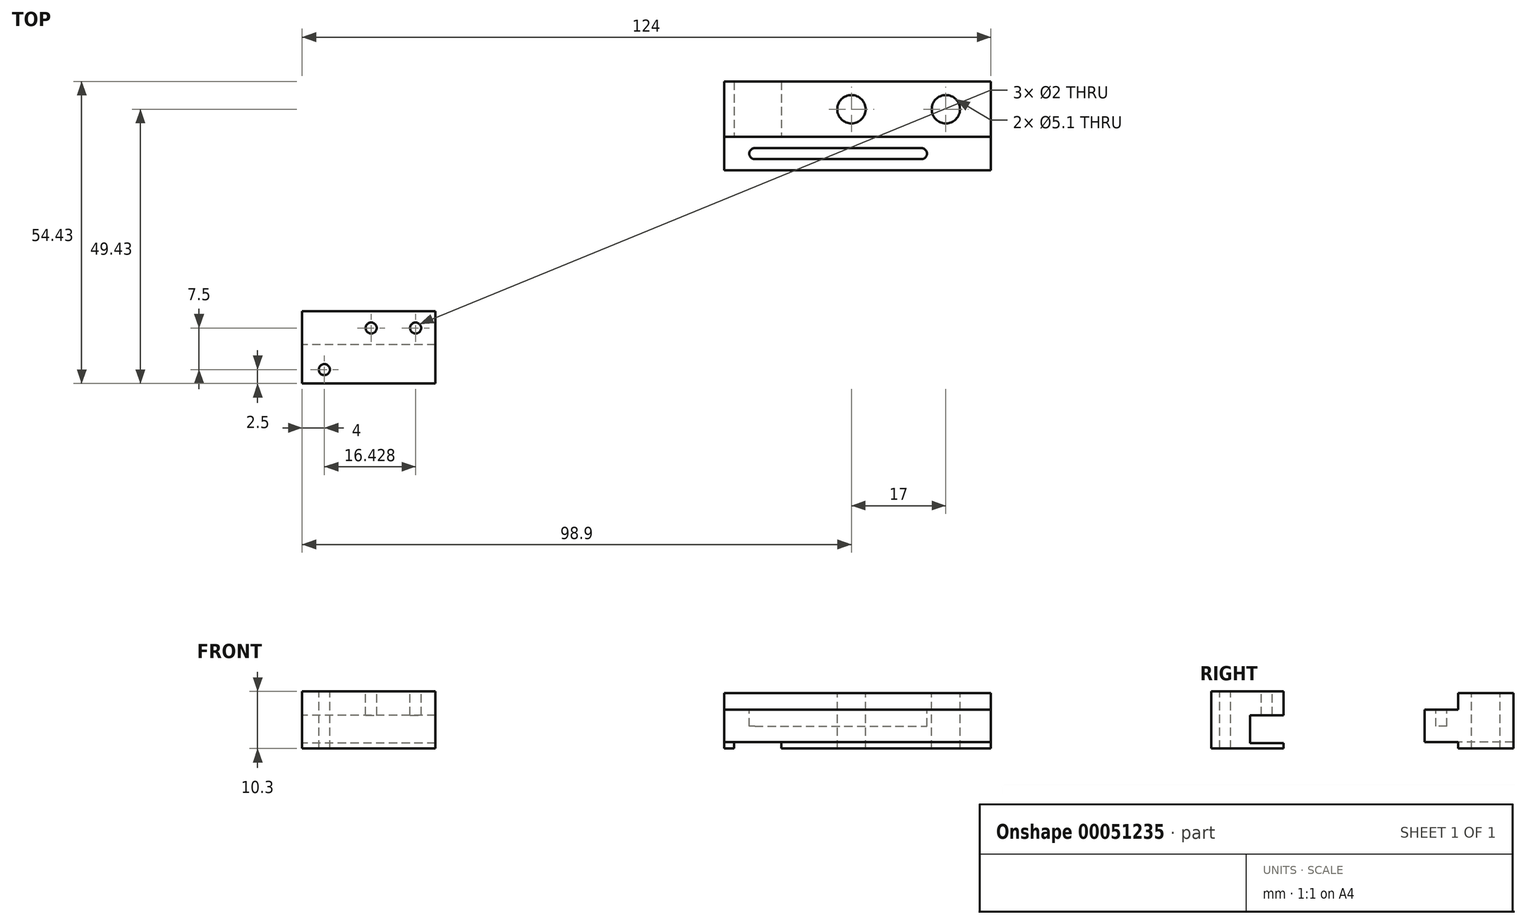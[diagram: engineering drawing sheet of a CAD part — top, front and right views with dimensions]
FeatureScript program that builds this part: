
annotation { "Feature Type Name" : "Feature", "Feature Type Description" : "" }
export const myFeature = defineFeature(function(context is Context, id is Id, definition is map)
    precondition{}
    {
        {
            var Q0;
            Q0=qCreatedBy(makeId("Right.planeOp"),FACE);
            var sketch = newSketch(context, id + "F0", { "sketchPlane" : qUnion([Q0])});
            skLineSegment(sketch, "E0", {"start": v(8, 0) * mm, "end": v(-2, 0) * mm});
            skLineSegment(sketch, "E1.0", {"start": v(8, 10) * mm, "end": v(-2, 10) * mm});
            skLineSegment(sketch, "E2", {"start": v(0, 0) * mm, "end": v(0, 15.1) * mm, "construction": true});
            skLineSegment(sketch, "E3.0", {"start": v(-8, 1.15) * mm, "end": v(-8, 7) * mm});
            skLineSegment(sketch, "E4.0", {"start": v(8, 0) * mm, "end": v(8, 10) * mm});
            skPoint(sketch, "E5.orphan", {"position": v(28.43, 0) * mm});
            skLineSegment(sketch, "E6.0", {"start": v(-2, 1.15) * mm, "end": v(-8, 1.15) * mm});
            skLineSegment(sketch, "E7.0", {"start": v(-2, 0) * mm, "end": v(-2, 1.15) * mm});
            skLineSegment(sketch, "E8", {"start": v(-2, 10) * mm, "end": v(-2, 7) * mm});
            skLineSegment(sketch, "E9", {"start": v(-2, 7) * mm, "end": v(-8, 7) * mm});
            skSolve(sketch);
        }
        {
            var Q0;
            Q0=makeQuery(id+"F0.imprint","IMPRINT",FACE,{"disambiguationData":[TD([[makeQuery(id+"F0.imprint","IMPRINT",EDGE,{"derivedFrom":sQuery(id+"F0.wireOp",EDGE,"E0")}),-1.0]])]});
            extrude(context, id + "F1", {"entities" : qUnion([Q0]), "endBound" : BoundingType.SYMMETRIC, "depth" : 48 * mm});
        }
        {
            var Q0;
            Q0=makeQuery(id+"F1.opExtrude","SWEPT_FACE",FACE,{"disambiguationData":[OSD([sQuery(id+"F0.wireOp",EDGE,"E1.0")])]});
            var sketch = newSketch(context, id + "F2", { "sketchPlane" : qUnion([Q0])});
            skPoint(sketch, "E10", {"position": v(15.9, 3) * mm});
            skPoint(sketch, "E11", {"position": v(-1.1, 3) * mm});
            skPoint(sketch, "E12", {"position": v(11.5, -5) * mm});
            skPoint(sketch, "E13", {"position": v(-18.5, -5) * mm});
            skArc(sketch, "E14", {"start": v(11.5, -6) * mm, "mid": v(12.5, -5) * mm, "end": v(11.5, -4) * mm});
            skArc(sketch, "E15", {"start": v(-18.5, -4) * mm, "mid": v(-19.5, -5) * mm, "end": v(-18.5, -6) * mm});
            skLineSegment(sketch, "E16", {"start": v(-18.5, -5) * mm, "end": v(11.5, -5) * mm, "construction": true});
            skLineSegment(sketch, "E17.0", {"start": v(-18.5, -6) * mm, "end": v(11.5, -6) * mm});
            skLineSegment(sketch, "E18.0", {"start": v(-18.5, -4) * mm, "end": v(11.5, -4) * mm});
            skSolve(sketch);
        }
        {
            var Q0;
            Q0=sQuery(id+"F2.wireOp",VERTEX,"E10");
            var Q1;
            Q1=sQuery(id+"F2.wireOp",VERTEX,"E11");
            var Q2;
            Q2=makeQuery(id+"F1.opExtrude","SWEPT_BODY",BODY,{"disambiguationData":[OSD([sQuery(id+"F0.wireOp",EDGE,"E0"),sQuery(id+"F0.wireOp",EDGE,"E1.0"),sQuery(id+"F0.wireOp",EDGE,"E3.0"),sQuery(id+"F0.wireOp",EDGE,"E4.0"),sQuery(id+"F0.wireOp",EDGE,"E6.0"),sQuery(id+"F0.wireOp",EDGE,"E7.0")])]});
            hole(context, id + "F3", {"style" : HoleStyle.SIMPLE, "holeDiameter" : 5.1 * mm, "endStyle" : HoleEndStyle.THROUGH, "locations" : qUnion([Q0, Q1]), "scope" : qUnion([Q2])});
        }
        {
            var Q0;
            Q0=makeQuery(id+"F1.opExtrude","SWEPT_FACE",FACE,{"disambiguationData":[OSD([sQuery(id+"F0.wireOp",EDGE,"E0")])]});
            var sketch = newSketch(context, id + "F4", { "sketchPlane" : qUnion([Q0])});
            skLineSegment(sketch, "E19.0", {"start": v(-22.2, -8) * mm, "end": v(-22.2, 2) * mm});
            skLineSegment(sketch, "E20.0", {"start": v(-13.7, -8) * mm, "end": v(-13.7, 2) * mm});
            skSolve(sketch);
        }
        {
            var Q0;
            {var subQ0=sQuery(id+"F4.wireOp",EDGE,"E19.0");Q0=makeQuery(id+"F4.imprint","IMPRINT",FACE,{"disambiguationData":[TD([[makeQuery(id+"F4.imprint","IMPRINT",EDGE,{"derivedFrom":subQ0}),-1.0]])]});}
            extrude(context, id + "F5", {"entities" : qUnion([Q0]), "operationType" : NewBodyOperationType.REMOVE, "oppositeDirection" : true, "depth" : 1.15 * mm});
        }
        {
            var Q0;
            Q0=makeQuery(id+"F2.imprint","IMPRINT",FACE,{"disambiguationData":[TD([[makeQuery(id+"F2.imprint","IMPRINT",EDGE,{"derivedFrom":sQuery(id+"F2.wireOp",EDGE,"E14")}),1.0]])]});
            extrude(context, id + "F6", {"entities" : qUnion([Q0]), "operationType" : NewBodyOperationType.REMOVE, "oppositeDirection" : true, "depth" : 6 * mm});
        }
        {
            var Q0;
            Q0=qCreatedBy(makeId("Right.planeOp"),FACE);
            cPlane(context, id + "F7", {"entities" : qUnion([Q0]), "cplaneType" : CPlaneType.OFFSET, "offset" : 100 * mm, "oppositeDirection" : true, "width" : 150 * mm, "height" : 150 * mm});
        }
        {
            var Q0;
            Q0=qCreatedBy(id+"F7.planeOp",FACE);
            var sketch = newSketch(context, id + "F8", { "sketchPlane" : qUnion([Q0])});
            skLineSegment(sketch, "E21", {"start": v(-33.43, 10.3) * mm, "end": v(-33.43, 6) * mm});
            skLineSegment(sketch, "E22", {"start": v(-33.43, 0) * mm, "end": v(-46.43, 0) * mm});
            skLineSegment(sketch, "E23.0", {"start": v(-33.43, 10.3) * mm, "end": v(-46.43, 10.3) * mm});
            skLineSegment(sketch, "E24.0", {"start": v(-46.43, 10.3) * mm, "end": v(-46.43, 0) * mm});
            skLineSegment(sketch, "E25.0", {"start": v(-39.43, 6) * mm, "end": v(-39.43, 1) * mm});
            skLineSegment(sketch, "E26.0", {"start": v(-33.43, 1) * mm, "end": v(-39.43, 1) * mm});
            skLineSegment(sketch, "E27.0", {"start": v(-33.43, 6) * mm, "end": v(-39.43, 6) * mm});
            skLineSegment(sketch, "E28.trimOffspring", {"start": v(-33.43, 1) * mm, "end": v(-33.43, 0) * mm});
            skPoint(sketch, "E29.orphan", {"position": v(-39.43, 10.3) * mm});
            skSolve(sketch);
        }
        {
            var Q0;
            Q0=makeQuery(id+"F8.imprint","IMPRINT",FACE,{"disambiguationData":[TD([[makeQuery(id+"F8.imprint","IMPRINT",EDGE,{"derivedFrom":sQuery(id+"F8.wireOp",EDGE,"E21")}),-1.0]])]});
            extrude(context, id + "F9", {"entities" : qUnion([Q0]), "depth" : 24 * mm});
        }
        {
            var Q0;
            Q0=makeQuery(id+"F9.opExtrude","SWEPT_FACE",FACE,{"disambiguationData":[OSD([sQuery(id+"F8.wireOp",EDGE,"E23.0")])]});
            var sketch = newSketch(context, id + "F10", { "sketchPlane" : qUnion([Q0])});
            skPoint(sketch, "E30", {"position": v(-96, -43.93) * mm});
            skPoint(sketch, "E31", {"position": v(-79.57, -36.43) * mm});
            skPoint(sketch, "E32", {"position": v(-87.57, -36.43) * mm});
            skCircle(sketch, "E33", {"center": v(-79.57, -36.43) * mm, "radius": 1 * mm});
            skCircle(sketch, "E34", {"center": v(-87.57, -36.43) * mm, "radius": 1 * mm});
            skCircle(sketch, "E35", {"center": v(-96, -43.93) * mm, "radius": 1 * mm});
            skSolve(sketch);
        }
        {
            var Q0;
            Q0=makeQuery(id+"F10.imprint","IMPRINT",FACE,{"disambiguationData":[TD([[makeQuery(id+"F10.imprint","IMPRINT",EDGE,{"derivedFrom":sQuery(id+"F10.wireOp",EDGE,"E33")}),1.0]])]});
            var Q1;
            Q1=makeQuery(id+"F10.imprint","IMPRINT",FACE,{"disambiguationData":[TD([[makeQuery(id+"F10.imprint","IMPRINT",EDGE,{"derivedFrom":sQuery(id+"F10.wireOp",EDGE,"E34")}),1.0]])]});
            var Q2;
            Q2=makeQuery(id+"F10.imprint","IMPRINT",FACE,{"disambiguationData":[TD([[makeQuery(id+"F10.imprint","IMPRINT",EDGE,{"derivedFrom":sQuery(id+"F10.wireOp",EDGE,"E35")}),1.0]])]});
            extrude(context, id + "F11", {"entities" : qUnion([Q0, Q1, Q2]), "operationType" : NewBodyOperationType.REMOVE, "endBound" : BoundingType.UP_TO_NEXT, "oppositeDirection" : true, "depth" : 25 * mm});
        }
    });
